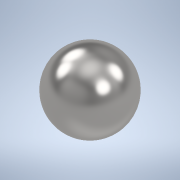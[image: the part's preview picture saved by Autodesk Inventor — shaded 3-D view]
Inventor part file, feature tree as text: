
AUTODESK INVENTOR PART (.ipt)
format: ipt  version: 2020 (Build 240168000, 168)  size: 122,880 bytes
history: native  units: in
note: dims shown in document units (in); Inventor stores cm internally (conversion verified against a paired STEP export)
features: revolve x1, sketch x1
ambient origin geometry x8: Origin, YZ Plane, XZ Plane, XY Plane, X Axis, Y Axis, Z Axis, Center Point
bodies: Solid1 (feature_tree)
feature tree (2):
  revolve  "Revolution1"  Angle=90.0deg
  sketch  "Sketch1"  dims[d0=0.0625in d1=90.0deg]
